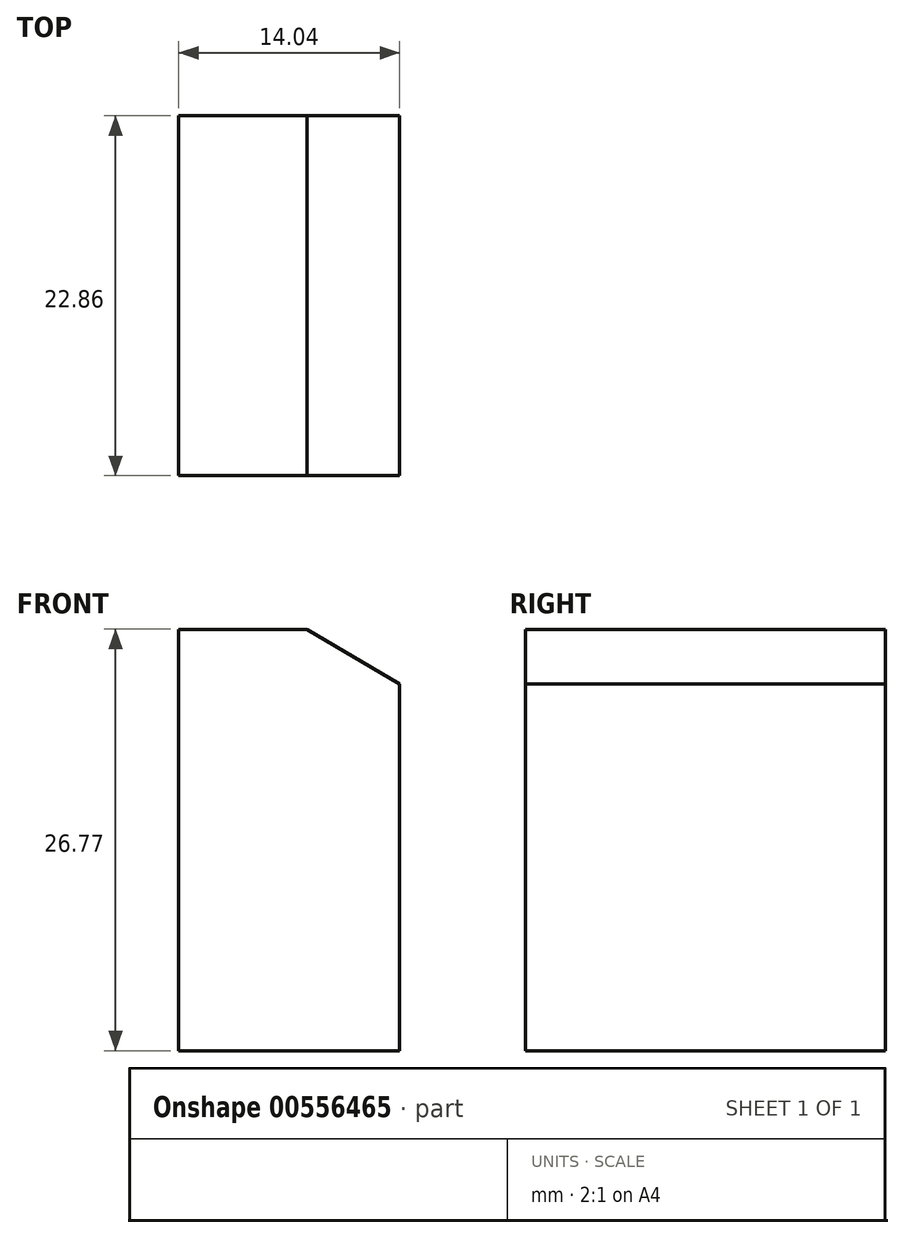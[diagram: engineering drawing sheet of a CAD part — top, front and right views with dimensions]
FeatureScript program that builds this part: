
annotation { "Feature Type Name" : "Feature", "Feature Type Description" : "" }
export const myFeature = defineFeature(function(context is Context, id is Id, definition is map)
    precondition{}
    {
        {
            var Q0;
            Q0=qCreatedBy(makeId("Front.planeOp"),FACE);
            var sketch = newSketch(context, id + "F0", { "sketchPlane" : qUnion([Q0])});
            skLineSegment(sketch, "E0", {"start": v(-24.15, 0) * mm, "end": v(-24.15, 26.77) * mm});
            skLineSegment(sketch, "E1", {"start": v(-24.15, 26.77) * mm, "end": v(-15.98, 26.77) * mm});
            skLineSegment(sketch, "E2", {"start": v(-15.98, 26.77) * mm, "end": v(-10.1, 23.28) * mm});
            skLineSegment(sketch, "E3", {"start": v(-10.1, 23.28) * mm, "end": v(-10.1, 0) * mm});
            skLineSegment(sketch, "E4", {"start": v(-15.98, 12.48) * mm, "end": v(-15.98, 0) * mm});
            skLineSegment(sketch, "E5", {"start": v(-12.92, 0) * mm, "end": v(-12.92, 11.58) * mm});
            skLineSegment(sketch, "E6", {"start": v(-24.15, 0) * mm, "end": v(-15.98, 0) * mm});
            skLineSegment(sketch, "E7", {"start": v(-12.92, 0) * mm, "end": v(-10.1, 0) * mm});
            skLineSegment(sketch, "E8", {"start": v(-15.98, 0) * mm, "end": v(-12.92, 0) * mm});
            skLineSegment(sketch, "E9", {"start": v(-15.98, 12.48) * mm, "end": v(-15.98, 20.86) * mm});
            skLineSegment(sketch, "E10", {"start": v(-16, 21.26) * mm, "end": v(-13.04, 25.02) * mm});
            skLineSegment(sketch, "E11", {"start": v(-12.92, 11.58) * mm, "end": v(-12.92, 20.45) * mm});
            skLineSegment(sketch, "E12", {"start": v(-12.92, 20.45) * mm, "end": v(-10.14, 23.3) * mm});
            skSolve(sketch);
        }
        {
            var Q0;
            Q0 = qSketchRegion(id + "F0", true);
            extrude(context, id + "F1", {"entities" : qUnion([Q0]), "depth" : 22.86 * mm, "offsetDistance" : 25.4 * mm});
        }
    });
